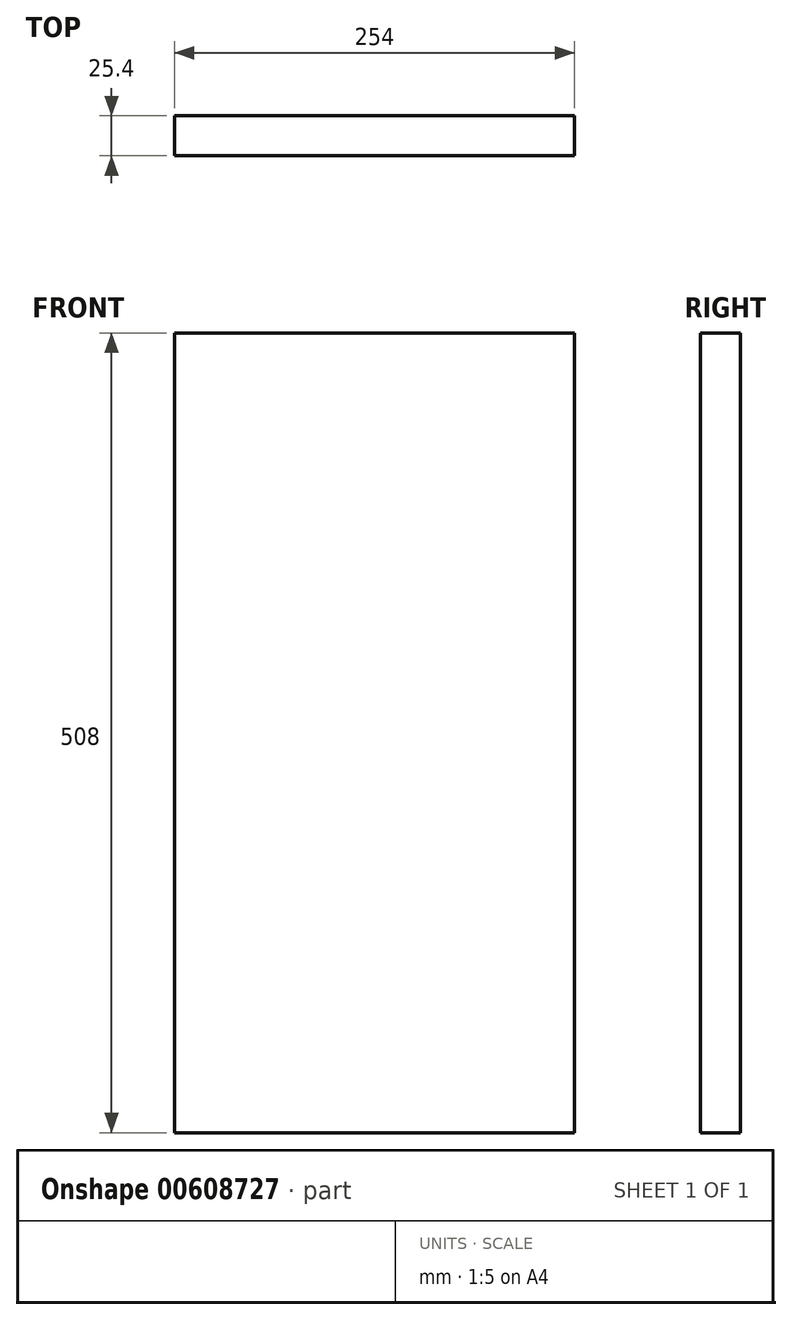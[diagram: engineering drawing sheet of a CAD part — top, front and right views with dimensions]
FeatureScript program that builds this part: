
annotation { "Feature Type Name" : "Feature", "Feature Type Description" : "" }
export const myFeature = defineFeature(function(context is Context, id is Id, definition is map)
    precondition{}
    {
        {
            var Q0;
            Q0=qCreatedBy(makeId("Front.planeOp"),FACE);
            var sketch = newSketch(context, id + "F0", { "sketchPlane" : qUnion([Q0])});
            skLineSegment(sketch, "E0.bottom", {"start": v(-197.84, 217.41) * mm, "end": v(56.16, 217.41) * mm});
            skLineSegment(sketch, "E0.top", {"start": v(-197.84, -290.59) * mm, "end": v(56.16, -290.59) * mm});
            skLineSegment(sketch, "E0.left", {"start": v(-197.84, 217.41) * mm, "end": v(-197.84, -290.59) * mm});
            skLineSegment(sketch, "E0.right", {"start": v(56.16, 217.41) * mm, "end": v(56.16, -290.59) * mm});
            skSolve(sketch);
        }
        {
            var Q0;
            Q0=makeQuery(id+"F0.imprint","IMPRINT",FACE,{"disambiguationData":[TD([[makeQuery(id+"F0.imprint","IMPRINT",EDGE,{"derivedFrom":sQuery(id+"F0.wireOp",EDGE,"E0.bottom")}),-1.0]])]});
            extrude(context, id + "F1", {"entities" : qUnion([Q0]), "depth" : 25.4 * mm, "offsetDistance" : 25.4 * mm});
        }
    });
